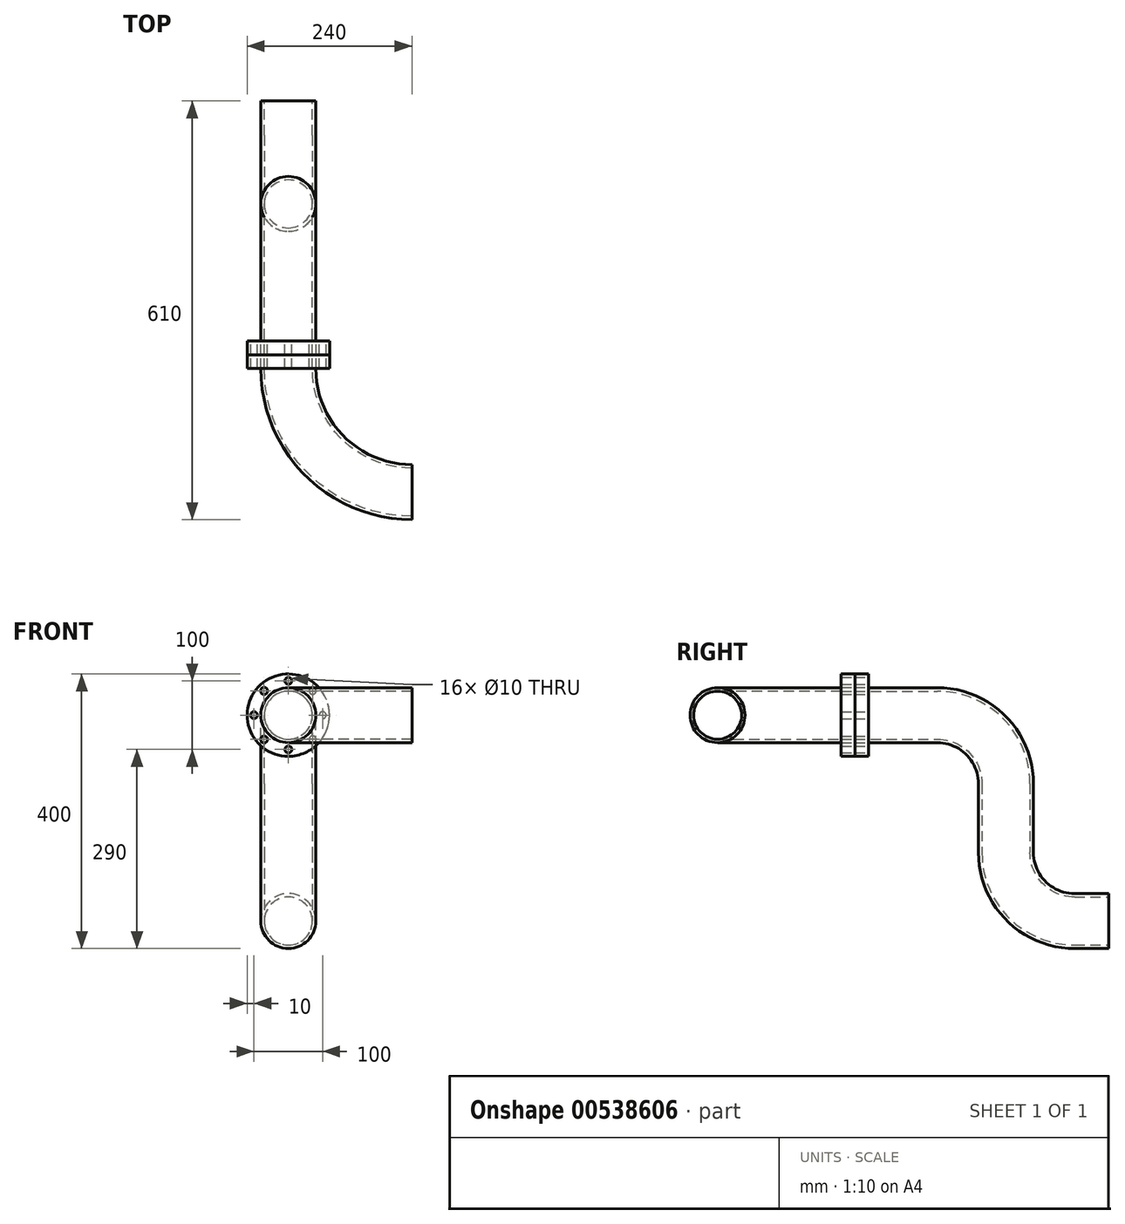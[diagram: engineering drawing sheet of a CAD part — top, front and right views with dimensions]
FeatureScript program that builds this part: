
annotation { "Feature Type Name" : "Feature", "Feature Type Description" : "" }
export const myFeature = defineFeature(function(context is Context, id is Id, definition is map)
    precondition{}
    {
        {
            var Q0;
            Q0=qCreatedBy(makeId("Front.planeOp"),FACE);
            var sketch = newSketch(context, id + "F0", { "sketchPlane" : qUnion([Q0])});
            skCircle(sketch, "E0", {"center": v(0, 0) * mm, "radius": 60 * mm});
            skCircle(sketch, "E1", {"center": v(0, 50) * mm, "radius": 5 * mm});
            skCircle(sketch, "E2.1.0", {"center": v(-35.36, 35.36) * mm, "radius": 5 * mm});
            skCircle(sketch, "E2.2.0", {"center": v(-50, 0) * mm, "radius": 5 * mm});
            skCircle(sketch, "E2.3.0", {"center": v(-35.36, -35.36) * mm, "radius": 5 * mm});
            skCircle(sketch, "E2.4.0", {"center": v(0, -50) * mm, "radius": 5 * mm});
            skCircle(sketch, "E2.5.0", {"center": v(35.36, -35.36) * mm, "radius": 5 * mm});
            skCircle(sketch, "E2.6.0", {"center": v(50, 0) * mm, "radius": 5 * mm});
            skCircle(sketch, "E2.7.0", {"center": v(35.36, 35.36) * mm, "radius": 5 * mm});
            skCircle(sketch, "E3", {"center": v(0, 0) * mm, "radius": 35 * mm});
            skSolve(sketch);
        }
        {
            var Q0;
            Q0=makeQuery(id+"F0.imprint","IMPRINT",FACE,{"disambiguationData":[TD([[makeQuery(id+"F0.imprint","IMPRINT",EDGE,{"derivedFrom":sQuery(id+"F0.wireOp",EDGE,"E0")}),1.0]])]});
            extrude(context, id + "F1", {"entities" : qUnion([Q0]), "depth" : 20 * mm, "offsetDistance" : 25 * mm});
        }
        {
            var Q0;
            Q0=qCreatedBy(makeId("Front.planeOp"),FACE);
            var sketch = newSketch(context, id + "F2", { "sketchPlane" : qUnion([Q0])});
            skCircle(sketch, "E4", {"center": v(0, 0) * mm, "radius": 40 * mm});
            skCircle(sketch, "E5", {"center": v(0, 0) * mm, "radius": 35 * mm});
            skSolve(sketch);
        }
        {
            var Q0;
            Q0=qCreatedBy(makeId("Right.planeOp"),FACE);
            var sketch = newSketch(context, id + "F3", { "sketchPlane" : qUnion([Q0])});
            skLineSegment(sketch, "E6", {"start": v(0, 0) * mm, "end": v(100, 0) * mm});
            skLineSegment(sketch, "E7", {"start": v(200, -100) * mm, "end": v(200, -200) * mm});
            skLineSegment(sketch, "E8", {"start": v(300, -300) * mm, "end": v(350, -300) * mm});
            skPoint(sketch, "E9.visualSharp", {"position": v(200, 0) * mm});
            skArc(sketch, "E9.filletArc", {"start": v(200, -100) * mm, "mid": v(170.71, -29.29) * mm, "end": v(100, 0) * mm});
            skPoint(sketch, "E10.visualSharp", {"position": v(200, -300) * mm});
            skArc(sketch, "E10.filletArc", {"start": v(200, -200) * mm, "mid": v(229.29, -270.71) * mm, "end": v(300, -300) * mm});
            skSolve(sketch);
        }
        {
            var Q0;
            Q0=makeQuery(id+"F2.imprint","IMPRINT",FACE,{"disambiguationData":[TD([[makeQuery(id+"F2.imprint","IMPRINT",EDGE,{"derivedFrom":sQuery(id+"F2.wireOp",EDGE,"E4")}),1.0]])]});
            var Q1;
            Q1 = qConstructionFilter(qBodyType(qCreatedBy(id + "F3" ,EDGE), BodyType.WIRE), ConstructionObject.NO);
            sweep(context, id + "F4", {"operationType" : NewBodyOperationType.ADD, "profiles" : qUnion([Q0]), "path" : qUnion([Q1])});
        }
        {
            var Q0;
            Q0=makeQuery(id+"F1.opExtrude","CAP_FACE",FACE,{"disambiguationData":[OSD([sQuery(id+"F0.wireOp",EDGE,"E0"),sQuery(id+"F0.wireOp",EDGE,"E1"),sQuery(id+"F0.wireOp",EDGE,"E2.1.0"),sQuery(id+"F0.wireOp",EDGE,"E2.2.0"),sQuery(id+"F0.wireOp",EDGE,"E2.3.0"),sQuery(id+"F0.wireOp",EDGE,"E2.4.0"),sQuery(id+"F0.wireOp",EDGE,"E2.5.0"),sQuery(id+"F0.wireOp",EDGE,"E2.6.0"),sQuery(id+"F0.wireOp",EDGE,"E2.7.0"),sQuery(id+"F0.wireOp",EDGE,"E3")])],"isStart":false});
            extrude(context, id + "F5", {"entities" : qUnion([Q0]), "depth" : 20 * mm, "offsetDistance" : 25 * mm});
        }
        {
            var Q0;
            Q0=makeQuery(id+"F5.opExtrude","CAP_FACE",FACE,{"disambiguationData":[OSD([sQuery(id+"F0.wireOp",EDGE,"E0"),sQuery(id+"F0.wireOp",EDGE,"E1"),sQuery(id+"F0.wireOp",EDGE,"E2.1.0"),sQuery(id+"F0.wireOp",EDGE,"E2.2.0"),sQuery(id+"F0.wireOp",EDGE,"E2.3.0"),sQuery(id+"F0.wireOp",EDGE,"E2.4.0"),sQuery(id+"F0.wireOp",EDGE,"E2.5.0"),sQuery(id+"F0.wireOp",EDGE,"E2.6.0"),sQuery(id+"F0.wireOp",EDGE,"E2.7.0"),sQuery(id+"F0.wireOp",EDGE,"E3")])],"isStart":false});
            var sketch = newSketch(context, id + "F6", { "sketchPlane" : qUnion([Q0])});
            skCircle(sketch, "E11", {"center": v(0, 0) * mm, "radius": 40 * mm});
            skCircle(sketch, "E12", {"center": v(0, 0) * mm, "radius": 35 * mm});
            skLineSegment(sketch, "E13", {"start": v(-100.39, 0) * mm, "end": v(110.66, 0) * mm, "construction": true});
            skLineSegment(sketch, "E14", {"start": v(180, 139.73) * mm, "end": v(180, -138.59) * mm, "construction": true});
            skSolve(sketch);
        }
        {
            var Q0;
            Q0 = qSketchRegion(id + "F6", true);
            var Q1;
            Q1=sQuery(id+"F6.wireOp",EDGE,"E14");
            revolve(context, id + "F7", {"operationType" : NewBodyOperationType.ADD, "entities" : qUnion([Q0]), "axis" : qUnion([Q1]), "revolveType" : RevolveType.ONE_DIRECTION, "oppositeDirection" : true, "angle" : 90 * degree});
        }
    });
